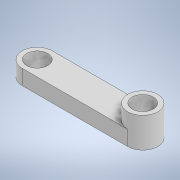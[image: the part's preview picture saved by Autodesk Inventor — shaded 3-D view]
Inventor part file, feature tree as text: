
AUTODESK INVENTOR PART (.ipt)
format: ipt  version: 2021 (Build 250183000, 183)  size: 116,736 bytes
history: native  units: mm
features: extrude x2, sketch x2
ambient origin geometry x8: Origin, YZ Plane, XZ Plane, XY Plane, X Axis, Y Axis, Z Axis, Center Point
bodies: Solid1 (feature_tree)
feature tree (4):
  extrude  "Extrusion1"  Depth=8.75mm
  extrude  "Extrusion2"  Depth=8.75mm
  sketch  "Sketch1"  dims[d0=8.75mm d1=3.5mm]
  sketch  "Sketch2"  dims[d2=5.0mm d3=8.75mm d4=3.5mm d5=5.0mm d6=2.5mm d7=0.0mm d8=5.0mm d9=2.5mm d10=0.0mm]
